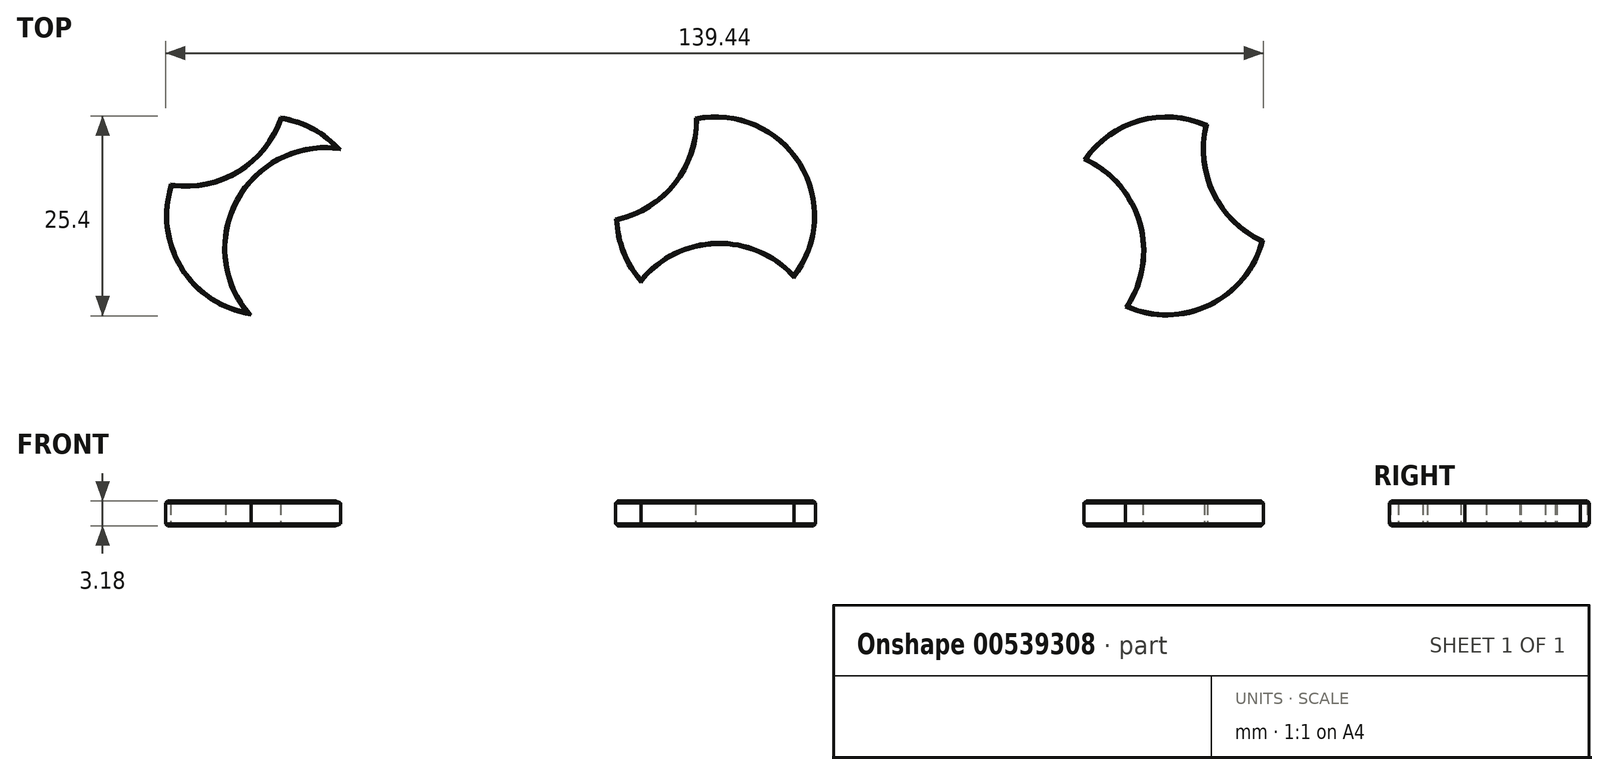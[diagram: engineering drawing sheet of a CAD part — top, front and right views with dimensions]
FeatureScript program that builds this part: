
annotation { "Feature Type Name" : "Feature", "Feature Type Description" : "" }
export const myFeature = defineFeature(function(context is Context, id is Id, definition is map)
    precondition{}
    {
        {
            var Q0;
            Q0=qCreatedBy(makeId("Top.planeOp"),FACE);
            var sketch = newSketch(context, id + "F0", { "sketchPlane" : qUnion([Q0])});
            skCircle(sketch, "E0", {"center": v(38.72, 0) * mm, "radius": 12.7 * mm, "construction": true});
            skCircle(sketch, "E1", {"center": v(-75.7, 0) * mm, "radius": 12.7 * mm, "construction": true});
            skCircle(sketch, "E2", {"center": v(-18.55, 0) * mm, "radius": 12.7 * mm, "construction": true});
            skPoint(sketch, "E3", {"position": v(28.22, 7.14) * mm});
            skPoint(sketch, "E4", {"position": v(43.93, 11.58) * mm});
            skPoint(sketch, "E5", {"position": v(51.03, -3.12) * mm});
            skPoint(sketch, "E6", {"position": v(33.5, -11.58) * mm});
            skPoint(sketch, "E7", {"position": v(-66.2, 8.41) * mm});
            skPoint(sketch, "E8", {"position": v(-77.59, -12.56) * mm});
            skPoint(sketch, "E9", {"position": v(-87.75, 4.03) * mm});
            skPoint(sketch, "E10", {"position": v(-73.83, 12.56) * mm});
            skPoint(sketch, "E11", {"position": v(-31.24, -0.36) * mm});
            skPoint(sketch, "E12", {"position": v(-28.04, -8.44) * mm});
            skPoint(sketch, "E13", {"position": v(-8.6, -7.88) * mm});
            skPoint(sketch, "E14", {"position": v(-21.11, 12.44) * mm});
            skLineSegment(sketch, "E15", {"start": v(38.72, 0) * mm, "end": v(28.22, 7.14) * mm, "construction": true});
            skLineSegment(sketch, "E16", {"start": v(43.93, 11.58) * mm, "end": v(38.72, 0) * mm, "construction": true});
            skLineSegment(sketch, "E17", {"start": v(38.72, 0) * mm, "end": v(51.03, -3.12) * mm, "construction": true});
            skLineSegment(sketch, "E18", {"start": v(38.72, 0) * mm, "end": v(33.5, -11.58) * mm, "construction": true});
            skLineSegment(sketch, "E19", {"start": v(-66.2, 8.41) * mm, "end": v(-75.7, 0) * mm, "construction": true});
            skLineSegment(sketch, "E20", {"start": v(-77.59, -12.56) * mm, "end": v(-75.7, 0) * mm, "construction": true});
            skLineSegment(sketch, "E21", {"start": v(-87.75, 4.03) * mm, "end": v(-75.7, 0) * mm, "construction": true});
            skLineSegment(sketch, "E22", {"start": v(-73.83, 12.56) * mm, "end": v(-75.7, 0) * mm, "construction": true});
            skLineSegment(sketch, "E23", {"start": v(-31.24, -0.36) * mm, "end": v(-18.55, 0) * mm, "construction": true});
            skLineSegment(sketch, "E24", {"start": v(-28.04, -8.44) * mm, "end": v(-18.55, 0) * mm, "construction": true});
            skLineSegment(sketch, "E25", {"start": v(-8.6, -7.88) * mm, "end": v(-18.55, 0) * mm, "construction": true});
            skLineSegment(sketch, "E26", {"start": v(-21.11, 12.44) * mm, "end": v(-18.55, 0) * mm, "construction": true});
            skArc(sketch, "E27", {"start": v(33.5, -11.58) * mm, "mid": v(35.23, -0.99) * mm, "end": v(28.22, 7.14) * mm});
            skArc(sketch, "E28", {"start": v(43.93, 11.58) * mm, "mid": v(44.8, 2.94) * mm, "end": v(51.03, -3.12) * mm});
            skArc(sketch, "E29", {"start": v(28.22, 7.14) * mm, "mid": v(35.26, 12.22) * mm, "end": v(43.93, 11.58) * mm});
            skArc(sketch, "E30", {"start": v(51.03, -3.12) * mm, "mid": v(44.24, -11.44) * mm, "end": v(33.5, -11.58) * mm});
            skArc(sketch, "E31", {"start": v(-77.59, -12.56) * mm, "mid": v(-86.54, -6.63) * mm, "end": v(-87.75, 4.03) * mm});
            skArc(sketch, "E32", {"start": v(-66.2, 8.41) * mm, "mid": v(-69.65, 11.16) * mm, "end": v(-73.83, 12.56) * mm});
            skArc(sketch, "E33", {"start": v(-66.2, 8.41) * mm, "mid": v(-79.23, 1.91) * mm, "end": v(-77.59, -12.56) * mm});
            skArc(sketch, "E34", {"start": v(-87.75, 4.03) * mm, "mid": v(-79.24, 5.76) * mm, "end": v(-73.83, 12.56) * mm});
            skArc(sketch, "E35", {"start": v(-8.6, -7.88) * mm, "mid": v(-7.74, 6.66) * mm, "end": v(-21.11, 12.44) * mm});
            skArc(sketch, "E36", {"start": v(-31.24, -0.36) * mm, "mid": v(-30.35, -4.68) * mm, "end": v(-28.04, -8.44) * mm});
            skArc(sketch, "E37", {"start": v(-8.6, -7.88) * mm, "mid": v(-18.44, -3.63) * mm, "end": v(-28.04, -8.44) * mm});
            skArc(sketch, "E38", {"start": v(-31.24, -0.36) * mm, "mid": v(-23.85, 4.2) * mm, "end": v(-21.11, 12.44) * mm});
            skSolve(sketch);
        }
        {
            var Q0;
            Q0 = qSketchRegion(id + "F0", true);
            extrude(context, id + "F1", {"entities" : qUnion([Q0]), "depth" : 3.17 * mm, "offsetDistance" : 25.4 * mm, "hasSecondDirection" : true, "secondDirectionOppositeDirection" : false, "secondDirectionDepth" : -2.38 * mm, "symmetric" : true});
        }
        {
            var Q0;
            Q0=makeQuery(id+"F1.opExtrude","CAP_FACE",FACE,{"disambiguationData":[OSD([sQuery(id+"F0.wireOp",EDGE,"E31"),sQuery(id+"F0.wireOp",EDGE,"E32"),sQuery(id+"F0.wireOp",EDGE,"E33"),sQuery(id+"F0.wireOp",EDGE,"E34")])],"isStart":false});
            var Q1;
            Q1=makeQuery(id+"F1.opExtrude","CAP_FACE",FACE,{"disambiguationData":[OSD([sQuery(id+"F0.wireOp",EDGE,"E31"),sQuery(id+"F0.wireOp",EDGE,"E32"),sQuery(id+"F0.wireOp",EDGE,"E33"),sQuery(id+"F0.wireOp",EDGE,"E34")])],"isStart":true});
            var Q2;
            Q2=makeQuery(id+"F1.opExtrude","CAP_FACE",FACE,{"disambiguationData":[OSD([sQuery(id+"F0.wireOp",EDGE,"E35"),sQuery(id+"F0.wireOp",EDGE,"E36"),sQuery(id+"F0.wireOp",EDGE,"E37"),sQuery(id+"F0.wireOp",EDGE,"E38")])],"isStart":false});
            var Q3;
            Q3=makeQuery(id+"F1.opExtrude","CAP_FACE",FACE,{"disambiguationData":[OSD([sQuery(id+"F0.wireOp",EDGE,"E35"),sQuery(id+"F0.wireOp",EDGE,"E36"),sQuery(id+"F0.wireOp",EDGE,"E37"),sQuery(id+"F0.wireOp",EDGE,"E38")])],"isStart":true});
            var Q4;
            Q4=makeQuery(id+"F1.opExtrude","CAP_FACE",FACE,{"disambiguationData":[OSD([sQuery(id+"F0.wireOp",EDGE,"E27"),sQuery(id+"F0.wireOp",EDGE,"E28"),sQuery(id+"F0.wireOp",EDGE,"E29"),sQuery(id+"F0.wireOp",EDGE,"E30")])],"isStart":false});
            var Q5;
            Q5=makeQuery(id+"F1.opExtrude","CAP_FACE",FACE,{"disambiguationData":[OSD([sQuery(id+"F0.wireOp",EDGE,"E27"),sQuery(id+"F0.wireOp",EDGE,"E28"),sQuery(id+"F0.wireOp",EDGE,"E29"),sQuery(id+"F0.wireOp",EDGE,"E30")])],"isStart":true});
            var Q6;
            Q6=makeQuery(id+"F2.opExtrude","CAP_EDGE",EDGE,{"disambiguationData":[OSD([sQuery(id+"FDYHwTi4w3c2tBF_3.wireOp",EDGE,"TkpoV5QC-uGwn-69Mv-bfU8-Rs0P5RJYmeZj")])],"isStart":false});
            var Q7;
            Q7=makeQuery(id+"F2.opExtrude","CAP_EDGE",EDGE,{"disambiguationData":[OSD([sQuery(id+"FDYHwTi4w3c2tBF_3.wireOp",EDGE,"TkpoV5QC-uGwn-69Mv-bfU8-Rs0P5RJYmeZj")])],"isStart":true});
            var Q8;
            Q8=makeQuery(id+"F2.opExtrude","CAP_EDGE",EDGE,{"disambiguationData":[OSD([sQuery(id+"FDYHwTi4w3c2tBF_3.wireOp",EDGE,"XTDZ4BZr-fd80-akWJ-m7xb-mUPJ6vjOCQB1")])],"isStart":false});
            var Q9;
            Q9=makeQuery(id+"F2.opExtrude","CAP_EDGE",EDGE,{"disambiguationData":[OSD([sQuery(id+"FDYHwTi4w3c2tBF_3.wireOp",EDGE,"XTDZ4BZr-fd80-akWJ-m7xb-mUPJ6vjOCQB1")])],"isStart":true});
            var Q10;
            Q10=makeQuery(id+"F2.opExtrude","CAP_EDGE",EDGE,{"disambiguationData":[OSD([sQuery(id+"FDYHwTi4w3c2tBF_3.wireOp",EDGE,"WO2pGQBS-OlN4-0PGy-hOrF-DOK9Omp8qCSG")])],"isStart":false});
            var Q11;
            Q11=makeQuery(id+"F2.opExtrude","CAP_EDGE",EDGE,{"disambiguationData":[OSD([sQuery(id+"FDYHwTi4w3c2tBF_3.wireOp",EDGE,"WO2pGQBS-OlN4-0PGy-hOrF-DOK9Omp8qCSG")])],"isStart":true});
            var Q12;
            Q12=makeQuery(id+"F2.opExtrude","CAP_EDGE",EDGE,{"disambiguationData":[OSD([sQuery(id+"FDYHwTi4w3c2tBF_3.wireOp",EDGE,"FcqKxZLc-rezC-QSwD-g4SZ-I11tKcFwuTGX")])],"isStart":false});
            var Q13;
            Q13=makeQuery(id+"F2.opExtrude","CAP_EDGE",EDGE,{"disambiguationData":[OSD([sQuery(id+"FDYHwTi4w3c2tBF_3.wireOp",EDGE,"FcqKxZLc-rezC-QSwD-g4SZ-I11tKcFwuTGX")])],"isStart":true});
            var Q14;
            Q14=makeQuery(id+"F2.opExtrude","CAP_EDGE",EDGE,{"disambiguationData":[OSD([sQuery(id+"FDYHwTi4w3c2tBF_3.wireOp",EDGE,"4kgWE4ok-ocKB-FhQ5-l9o4-UJoEO8jlKHbJ")])],"isStart":false});
            var Q15;
            Q15=makeQuery(id+"F2.opExtrude","CAP_EDGE",EDGE,{"disambiguationData":[OSD([sQuery(id+"FDYHwTi4w3c2tBF_3.wireOp",EDGE,"4kgWE4ok-ocKB-FhQ5-l9o4-UJoEO8jlKHbJ")])],"isStart":true});
            var Q16;
            Q16=makeQuery(id+"F2.opExtrude","CAP_EDGE",EDGE,{"disambiguationData":[OSD([sQuery(id+"FDYHwTi4w3c2tBF_3.wireOp",EDGE,"mE4zdYN1-UHLs-Q1cb-Ql1B-5NxPq1QZElJI")])],"isStart":false});
            var Q17;
            Q17=makeQuery(id+"F2.opExtrude","CAP_EDGE",EDGE,{"disambiguationData":[OSD([sQuery(id+"FDYHwTi4w3c2tBF_3.wireOp",EDGE,"mE4zdYN1-UHLs-Q1cb-Ql1B-5NxPq1QZElJI")])],"isStart":true});
            chamfer(context, id + "F3", {"entities" : qUnion([Q0, Q1, Q2, Q3, Q4, Q5, Q6, Q7, Q8, Q9, Q10, Q11, Q12, Q13, Q14, Q15, Q16, Q17]), "width" : 0.25 * mm, "tangentPropagation" : true});
        }
    });
